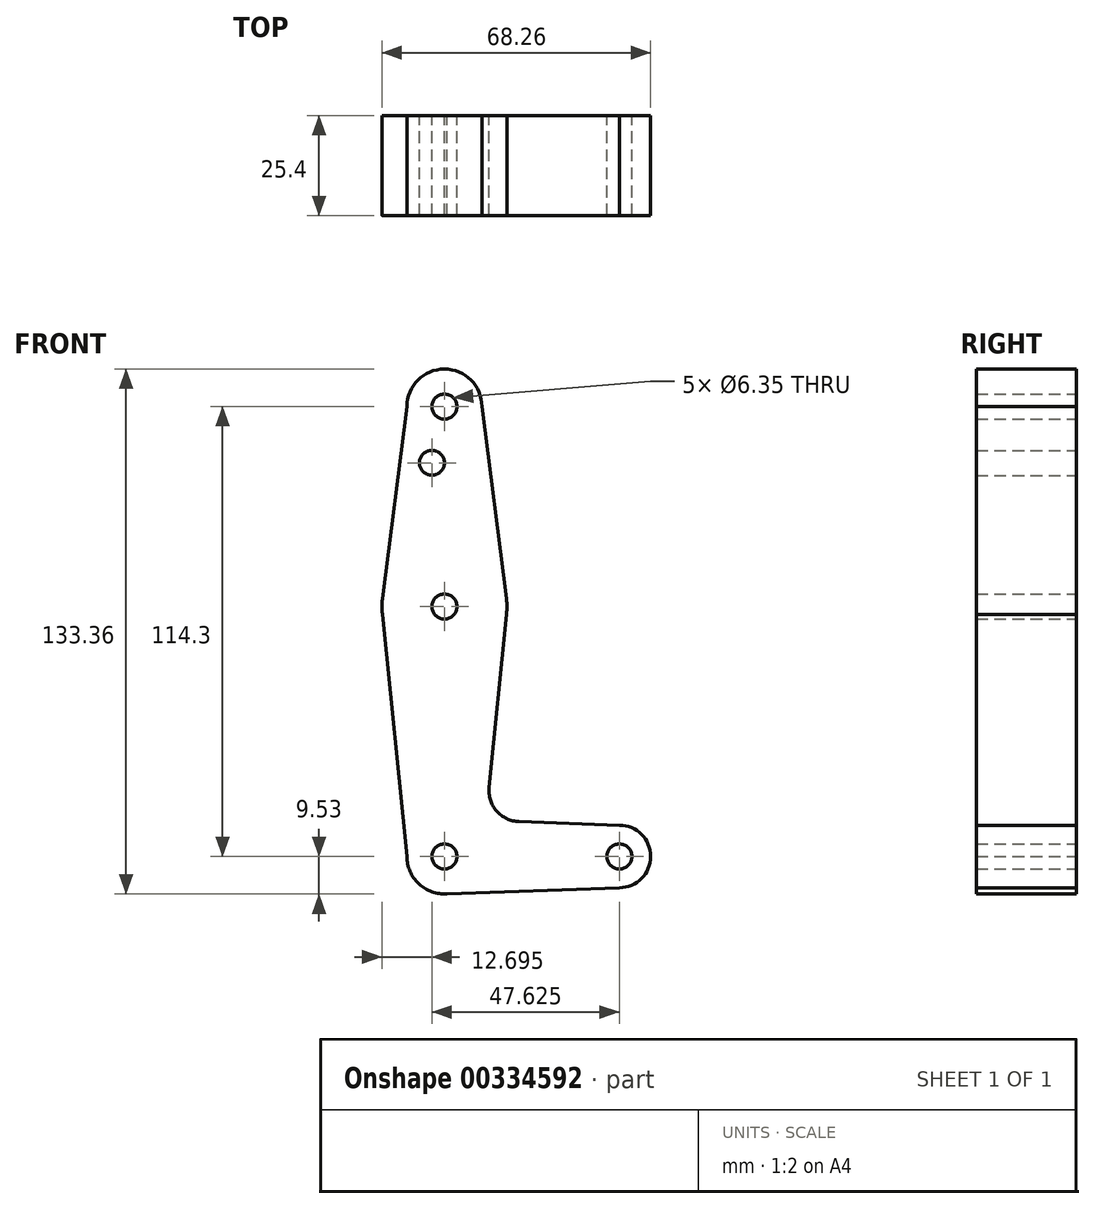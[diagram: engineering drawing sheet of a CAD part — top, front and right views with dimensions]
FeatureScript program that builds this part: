
annotation { "Feature Type Name" : "Feature", "Feature Type Description" : "" }
export const myFeature = defineFeature(function(context is Context, id is Id, definition is map)
    precondition{}
    {
        {
            var Q0;
            Q0=qCreatedBy(makeId("Front.planeOp"),FACE);
            var sketch = newSketch(context, id + "F0", { "sketchPlane" : qUnion([Q0])});
            skCircle(sketch, "E0", {"center": v(0, 0) * mm, "radius": 9.53 * mm});
            skCircle(sketch, "E1", {"center": v(44.45, 0) * mm, "radius": 7.94 * mm});
            skLineSegment(sketch, "E2", {"start": v(0, 0) * mm, "end": v(44.45, 0) * mm});
            skLineSegment(sketch, "E3", {"start": v(0, 0) * mm, "end": v(0, 114.3) * mm});
            skCircle(sketch, "E4", {"center": v(0, 114.3) * mm, "radius": 9.53 * mm});
            skCircle(sketch, "E5", {"center": v(0, 63.5) * mm, "radius": 15.88 * mm});
            skLineSegment(sketch, "E6", {"start": v(18.96, 8.85) * mm, "end": v(44.45, 7.94) * mm});
            skLineSegment(sketch, "E7", {"start": v(0, -9.53) * mm, "end": v(44.45, -7.94) * mm});
            skCircle(sketch, "E8", {"center": v(0, 114.3) * mm, "radius": 3.18 * mm});
            skCircle(sketch, "E9", {"center": v(0, 63.5) * mm, "radius": 3.18 * mm});
            skCircle(sketch, "E10", {"center": v(0, 0) * mm, "radius": 3.18 * mm});
            skCircle(sketch, "E11", {"center": v(44.45, 0) * mm, "radius": 3.18 * mm});
            skLineSegment(sketch, "E12", {"start": v(-9.53, 114.3) * mm, "end": v(-15.75, 65.5) * mm});
            skLineSegment(sketch, "E13", {"start": v(-15.75, 61.5) * mm, "end": v(-9.52, 0) * mm});
            skLineSegment(sketch, "E14", {"start": v(9.53, 114.3) * mm, "end": v(15.75, 65.5) * mm});
            skLineSegment(sketch, "E15", {"start": v(15.75, 61.5) * mm, "end": v(11.34, 17.6) * mm});
            skCircle(sketch, "E16", {"center": v(-3.18, 100.03) * mm, "radius": 3.18 * mm});
            skArc(sketch, "E17.filletArc", {"start": v(11.34, 17.6) * mm, "mid": v(13.26, 11.57) * mm, "end": v(18.96, 8.85) * mm});
            skSolve(sketch);
        }
        {
            var Q0;
            Q0 = qSketchRegion(id + "F0", true);
            var Q1;
            {var subQ0=sQuery(id+"F0.wireOp",EDGE,"E3");var subQ1=sQuery(id+"F0.wireOp",EDGE,"E0");var subQ2=makeQuery(id+"F0.imprint","INTERSECT",VERTEX,{"derivedFrom":[subQ1,subQ0]});Q1=makeQuery(id+"F0.imprint","IMPRINT",FACE,{"disambiguationData":[TD([[makeQuery(id+"F0.imprint","IMPRINT",EDGE,{"disambiguationData":[TD([[subQ2,1.0]])],"derivedFrom":subQ1}),1.0]])]});}
            extrude(context, id + "F1", {"entities" : qUnion([Q0, Q1]), "depth" : 25.4 * mm});
        }
    });
